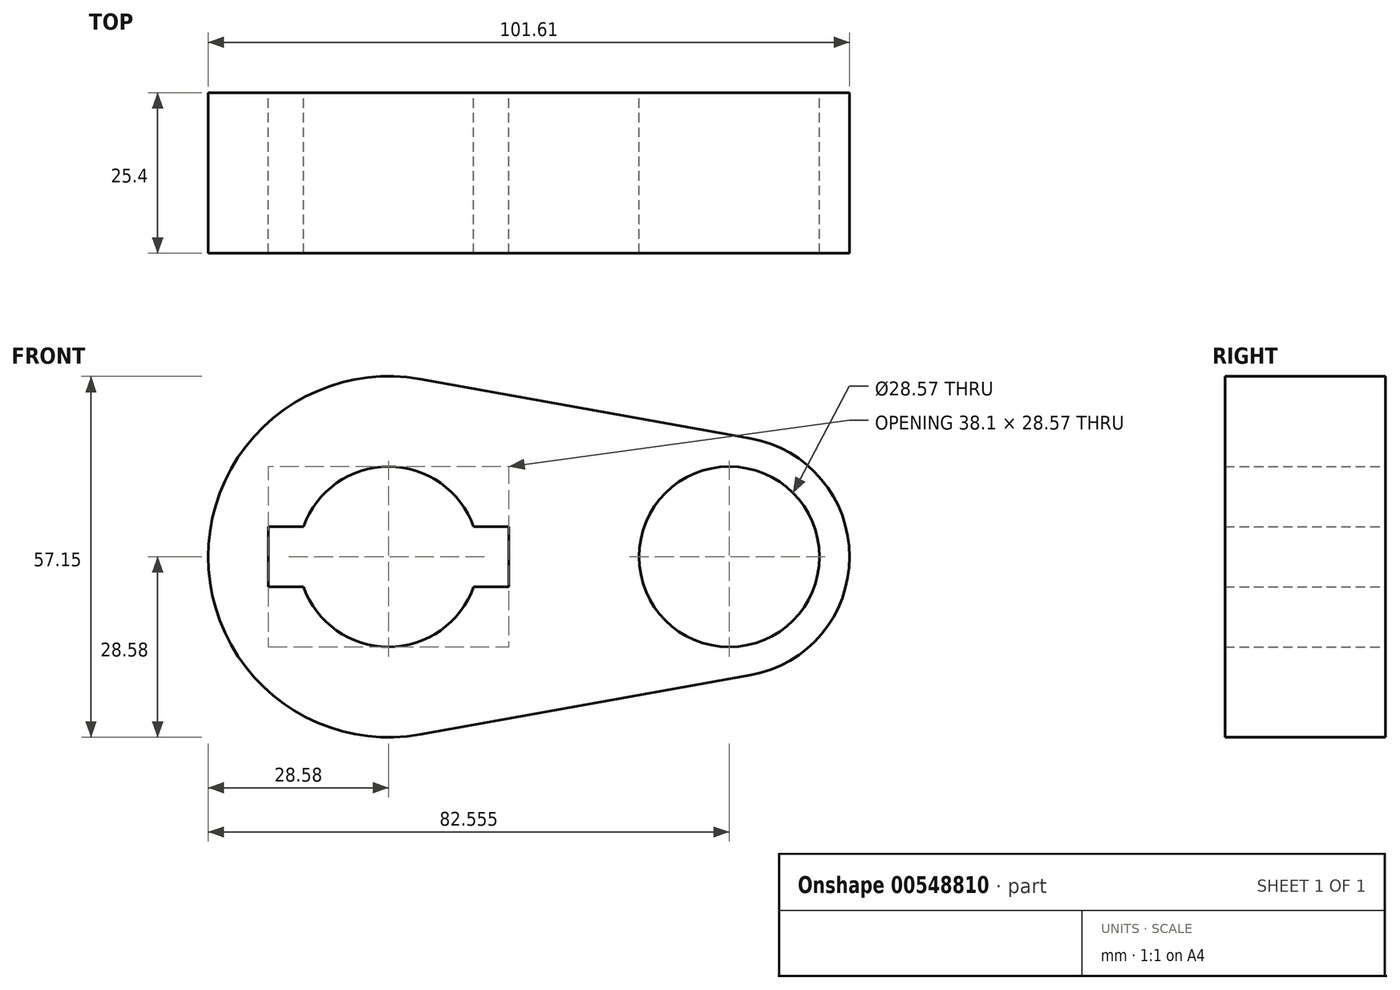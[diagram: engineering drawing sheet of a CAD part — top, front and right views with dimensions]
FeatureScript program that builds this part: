
annotation { "Feature Type Name" : "Feature", "Feature Type Description" : "" }
export const myFeature = defineFeature(function(context is Context, id is Id, definition is map)
    precondition{}
    {
        {
            var Q0;
            Q0=qCreatedBy(makeId("Front.planeOp"),FACE);
            var sketch = newSketch(context, id + "F0", { "sketchPlane" : qUnion([Q0])});
            skCircle(sketch, "E0", {"center": v(0, 0) * mm, "radius": 28.58 * mm});
            skCircle(sketch, "E1", {"center": v(53.98, 0) * mm, "radius": 19.05 * mm});
            skLineSegment(sketch, "E2", {"start": v(5.04, 28.13) * mm, "end": v(57.34, 18.75) * mm});
            skLineSegment(sketch, "E3", {"start": v(5.04, -28.13) * mm, "end": v(57.34, -18.75) * mm});
            skCircle(sketch, "E4", {"center": v(0, 0) * mm, "radius": 14.29 * mm});
            skCircle(sketch, "E5", {"center": v(53.98, 0) * mm, "radius": 14.29 * mm});
            skLineSegment(sketch, "E6.bottom", {"start": v(-19.05, -4.76) * mm, "end": v(19.05, -4.76) * mm});
            skLineSegment(sketch, "E6.top", {"start": v(-19.05, 4.76) * mm, "end": v(19.05, 4.76) * mm});
            skLineSegment(sketch, "E6.left", {"start": v(-19.05, -4.76) * mm, "end": v(-19.05, 4.76) * mm});
            skLineSegment(sketch, "E6.right", {"start": v(19.05, -4.76) * mm, "end": v(19.05, 4.76) * mm});
            skSolve(sketch);
        }
        {
            var Q0;
            {var subQ7=sQuery(id+"F0.wireOp",EDGE,"E6.left");Q0=makeQuery(id+"F0.imprint","IMPRINT",FACE,{"disambiguationData":[TD([[makeQuery(id+"F0.imprint","IMPRINT",EDGE,{"derivedFrom":subQ7}),1.0]])]});}
            var Q1;
            {var subQ0=sQuery(id+"F0.wireOp",EDGE,"E2");Q1=makeQuery(id+"F0.imprint","IMPRINT",FACE,{"disambiguationData":[TD([[makeQuery(id+"F0.imprint","IMPRINT",EDGE,{"derivedFrom":subQ0}),-1.0]])]});}
            var Q2;
            Q2=makeQuery(id+"F0.imprint","IMPRINT",FACE,{"disambiguationData":[TD([[makeQuery(id+"F0.imprint","IMPRINT",EDGE,{"derivedFrom":sQuery(id+"F0.wireOp",EDGE,"E5")}),-1.0]])]});
            extrude(context, id + "F1", {"entities" : qUnion([Q0, Q1, Q2]), "depth" : 25.4 * mm, "offsetDistance" : 25.4 * mm});
        }
    });
